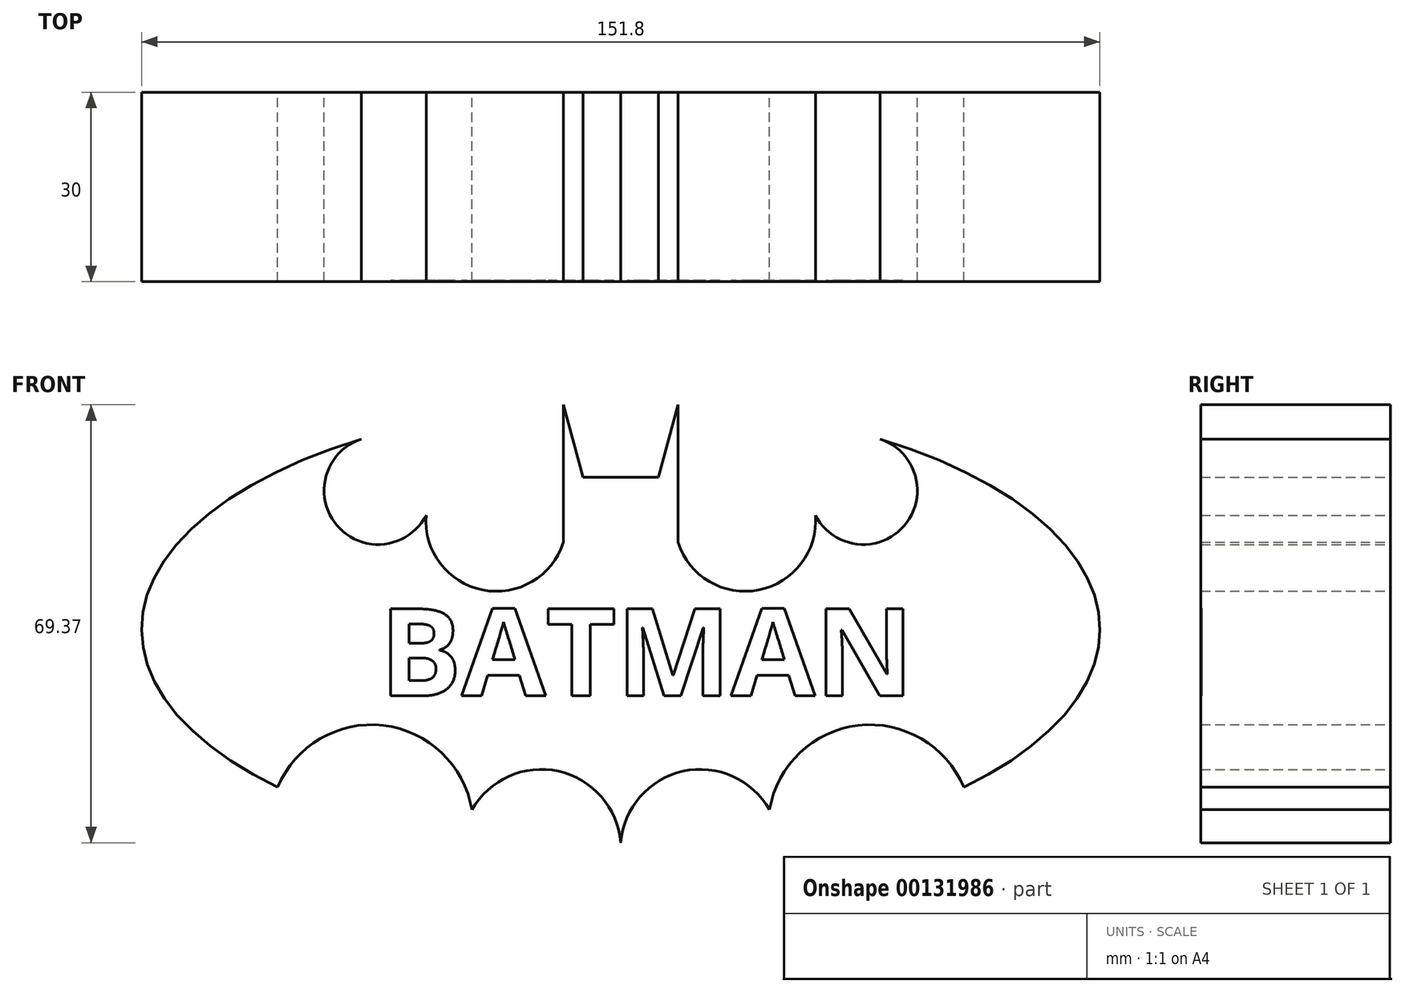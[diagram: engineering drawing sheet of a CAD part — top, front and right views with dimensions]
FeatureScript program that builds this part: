
annotation { "Feature Type Name" : "Feature", "Feature Type Description" : "" }
export const myFeature = defineFeature(function(context is Context, id is Id, definition is map)
    precondition{}
    {
        {
            var Q0;
            Q0=qCreatedBy(makeId("Front.planeOp"),FACE);
            var sketch = newSketch(context, id + "F0", { "sketchPlane" : qUnion([Q0])});
            skEllipticalArc(sketch, "E0", {});
            skLineSegment(sketch, "E1", {"start": v(-9.07, 35.57) * mm, "end": v(-5.96, 24.07) * mm});
            skLineSegment(sketch, "E2", {"start": v(-5.96, 24.07) * mm, "end": v(0, 24.12) * mm});
            skLineSegment(sketch, "E3.MirrorCS", {"start": v(9.07, 35.57) * mm, "end": v(5.96, 24.07) * mm});
            skLineSegment(sketch, "E4.MirrorCS", {"start": v(5.96, 24.07) * mm, "end": v(0, 24.12) * mm});
            skLineSegment(sketch, "E5", {"start": v(-9.07, 35.57) * mm, "end": v(-9.07, 13.77) * mm});
            skArc(sketch, "E6", {"start": v(-40.72, 30.23) * mm, "mid": v(-45.07, 16.6) * mm, "end": v(-30.83, 18.08) * mm});
            skPoint(sketch, "E6.first.point", {"position": v(-30.83, 18.08) * mm});
            skPoint(sketch, "E6.second.point", {"position": v(-46.87, 20.6) * mm});
            skPoint(sketch, "E6.third.point", {"position": v(-40.72, 30.23) * mm});
            skArc(sketch, "E7", {"start": v(0, -35.83) * mm, "mid": v(-8.88, -22.74) * mm, "end": v(-23.57, -28.58) * mm});
            skPoint(sketch, "E7.second.point", {"position": v(0, -35.83) * mm});
            skPoint(sketch, "E7.third.point", {"position": v(-11.27, -22.25) * mm});
            skPoint(sketch, "E8.first.point", {"position": v(-23.57, -28.58) * mm});
            skPoint(sketch, "E8.second.point", {"position": v(-54.33, -25.02) * mm});
            skArc(sketch, "E9.MirrorC", {"start": v(30.83, 18.08) * mm, "mid": v(21.87, 6.24) * mm, "end": v(9.07, 13.77) * mm});
            skArc(sketch, "E10.MirrorC", {"start": v(40.72, 30.23) * mm, "mid": v(45.07, 16.6) * mm, "end": v(30.83, 18.08) * mm});
            skArc(sketch, "E11.MirrorC", {"start": v(23.57, -28.58) * mm, "mid": v(37.6, -15.22) * mm, "end": v(54.33, -25.02) * mm});
            skArc(sketch, "E12.MirrorC", {"start": v(0, -35.83) * mm, "mid": v(8.88, -22.74) * mm, "end": v(23.57, -28.58) * mm});
            skLineSegment(sketch, "E13.MirrorCS", {"start": v(9.07, 35.57) * mm, "end": v(9.07, 13.77) * mm});
            skArc(sketch, "E14.trimOffspring", {"start": v(-30.83, 18.08) * mm, "mid": v(-21.87, 6.24) * mm, "end": v(-9.07, 13.77) * mm});
            skEllipticalArc(sketch, "E15.trimOffspring", {});
            skArc(sketch, "E16.trimOffspring", {"start": v(-23.57, -28.58) * mm, "mid": v(-37.6, -15.22) * mm, "end": v(-54.33, -25.02) * mm});
            const initialGuessF0  = {"E0": [0, 0, 1, 0, 0.07590328902006149, 0.03582748770713806, 2.1370947848208646, 3.9146955171802964], "E15.trimOffspring": [0, 0, 1, 0, 0.07590328902006149, 0.03582748770713806, 5.5100824435890825, 1.0094396120371805]};
            skSetInitialGuess(sketch, initialGuessF0);
            skSolve(sketch);
        }
        {
            var Q0;
            Q0=makeQuery(id+"F0.imprint","IMPRINT",FACE,{"disambiguationData":[TD([[makeQuery(id+"F0.imprint","IMPRINT",EDGE,{"derivedFrom":sQuery(id+"F0.wireOp",EDGE,"E1")}),-1.0]])]});
            extrude(context, id + "F1", {"entities" : qUnion([Q0]), "depth" : 30 * mm});
        }
        {
            var Q0;
            Q0=makeQuery(id+"F1.opExtrude","CAP_FACE",FACE,{"disambiguationData":[OSD([sQuery(id+"F0.wireOp",EDGE,"E0"),sQuery(id+"F0.wireOp",EDGE,"E1"),sQuery(id+"F0.wireOp",EDGE,"E2"),sQuery(id+"F0.wireOp",EDGE,"E3.MirrorCS"),sQuery(id+"F0.wireOp",EDGE,"E4.MirrorCS"),sQuery(id+"F0.wireOp",EDGE,"E5"),sQuery(id+"F0.wireOp",EDGE,"E6"),sQuery(id+"F0.wireOp",EDGE,"E7"),sQuery(id+"F0.wireOp",EDGE,"E9.MirrorC"),sQuery(id+"F0.wireOp",EDGE,"E10.MirrorC"),sQuery(id+"F0.wireOp",EDGE,"E11.MirrorC"),sQuery(id+"F0.wireOp",EDGE,"E12.MirrorC"),sQuery(id+"F0.wireOp",EDGE,"E13.MirrorCS"),sQuery(id+"F0.wireOp",EDGE,"E14.trimOffspring"),sQuery(id+"F0.wireOp",EDGE,"E15.trimOffspring"),sQuery(id+"F0.wireOp",EDGE,"E16.trimOffspring")])],"isStart":false});
            var sketch = newSketch(context, id + "F2", { "sketchPlane" : qUnion([Q0])});
            skText(sketch, "E17", { "text": "BATMAN", "fontName": "OpenSans-Bold.ttf"});
            const initialGuessF2  = {"E17": [-0.03817, -0.01053, 1, 0, 0.01389]};
            skSetInitialGuess(sketch, initialGuessF2);
            skSolve(sketch);
        }
        {
            var Q0;
            Q0 = qSketchRegion(id + "F2", true);
            extrude(context, id + "F3", {"entities" : qUnion([Q0]), "operationType" : NewBodyOperationType.REMOVE, "oppositeDirection" : true, "depth" : 0.2 * mm});
        }
    });
